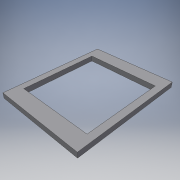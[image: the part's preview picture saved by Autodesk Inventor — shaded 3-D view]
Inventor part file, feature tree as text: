
AUTODESK INVENTOR PART (.ipt)
format: ipt  version: 2016 (Build 200138000, 138)  size: 98,816 bytes
history: native  units: in
note: dims shown in document units (in); Inventor stores cm internally (conversion verified against a paired STEP export)
features: extrude x2, sketch x2
ambient origin geometry x8: Origin, YZ Plane, XZ Plane, XY Plane, X Axis, Y Axis, Z Axis, Center Point
bodies: Solid1 (feature_tree)
feature tree (4):
  extrude  "Extrusion1"  Depth=16.0in
  extrude  "Extrusion2"  Depth=14.5in
  sketch  "Sketch1"  dims[d0=20.0in d1=16.0in]
  sketch  "Sketch2"  dims[d2=1.0in d3=0.0in d4=14.5in d5=13.5in d6=1.0in d7=0.0in]
